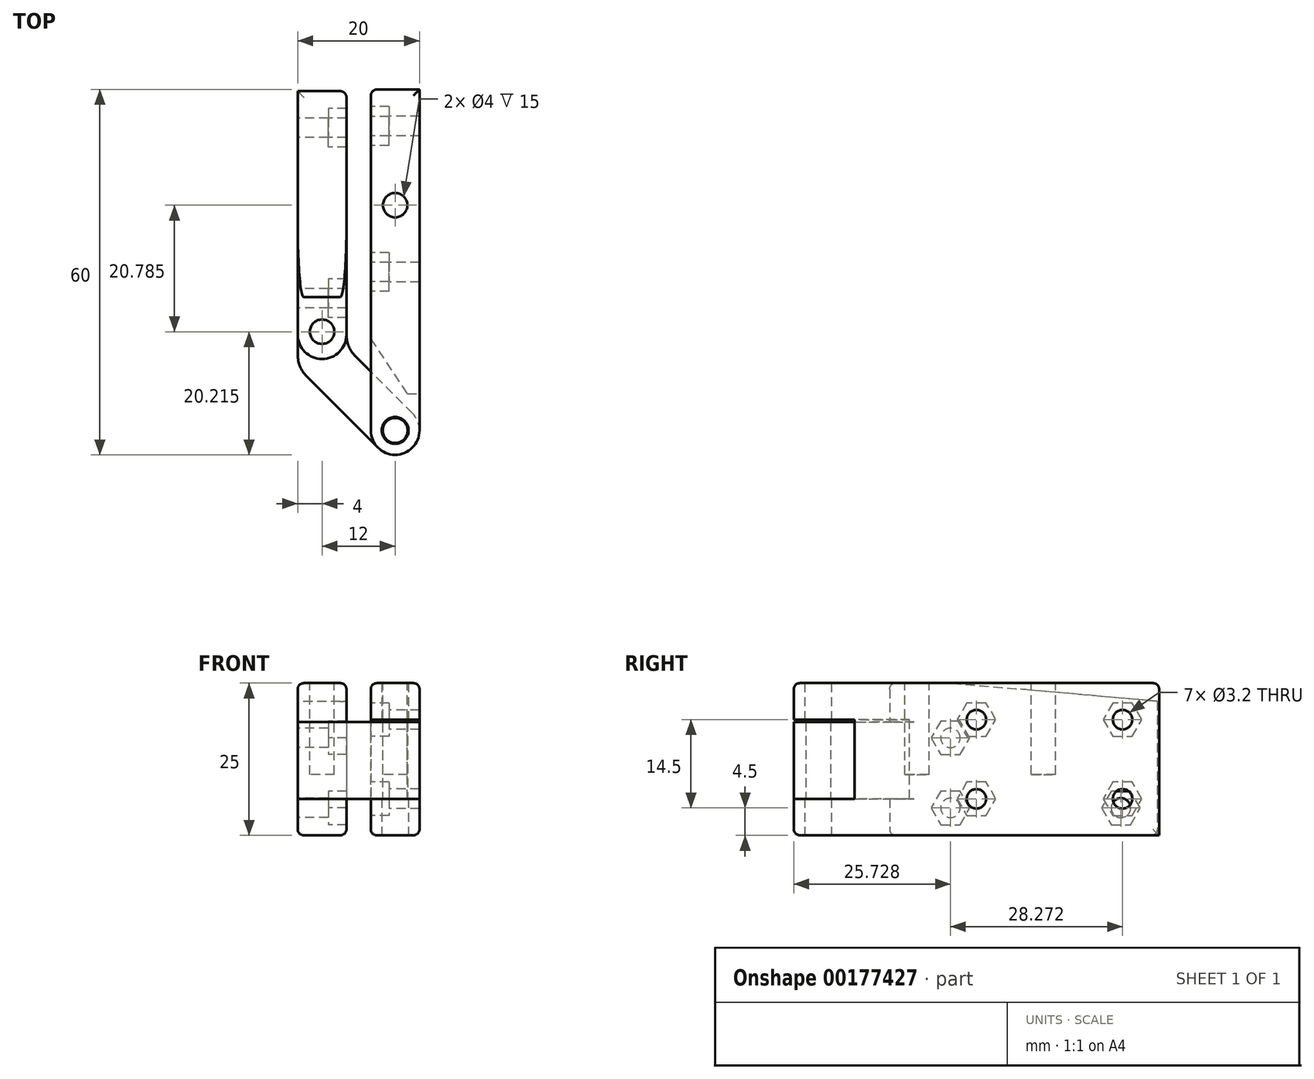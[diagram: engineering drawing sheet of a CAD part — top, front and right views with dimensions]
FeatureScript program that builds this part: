
annotation { "Feature Type Name" : "Feature", "Feature Type Description" : "" }
export const myFeature = defineFeature(function(context is Context, id is Id, definition is map)
    precondition{}
    {
        {
            var Q0;
            Q0=qCreatedBy(makeId("Top.planeOp"),FACE);
            var sketch = newSketch(context, id + "F0", { "sketchPlane" : qUnion([Q0])});
            skLineSegment(sketch, "E0", {"start": v(0, 0) * mm, "end": v(8, 0) * mm});
            skLineSegment(sketch, "E1", {"start": v(8, 0) * mm, "end": v(8, -42) * mm});
            skLineSegment(sketch, "E2", {"start": v(0, 0) * mm, "end": v(0, -42) * mm});
            skArc(sketch, "E3", {"start": v(0, -42) * mm, "mid": v(4, -46) * mm, "end": v(8, -42) * mm});
            skCircle(sketch, "E4", {"center": v(4, -42) * mm, "radius": 2.2 * mm});
            skLineSegment(sketch, "E5", {"start": v(0, 0) * mm, "end": v(0, 14) * mm});
            skLineSegment(sketch, "E6", {"start": v(0, 14) * mm, "end": v(8, 14) * mm});
            skLineSegment(sketch, "E7", {"start": v(8, 14) * mm, "end": v(8, 0) * mm});
            skSolve(sketch);
        }
        {
            var Q0;
            Q0=makeQuery(id+"F0.imprint","IMPRINT",FACE,{"disambiguationData":[TD([[makeQuery(id+"F0.imprint","IMPRINT",EDGE,{"derivedFrom":sQuery(id+"F0.wireOp",EDGE,"E0")}),-1.0]])]});
            var Q1;
            Q1=makeQuery(id+"F0.imprint","IMPRINT",FACE,{"disambiguationData":[TD([[makeQuery(id+"F0.imprint","IMPRINT",EDGE,{"derivedFrom":sQuery(id+"F0.wireOp",EDGE,"E0")}),1.0]])]});
            extrude(context, id + "F1", {"entities" : qUnion([Q0, Q1]), "depth" : 25 * mm});
        }
        {
            var Q0;
            Q0=makeQuery(id+"F1.opExtrude","SWEPT_FACE",FACE,{"disambiguationData":[OSD([sQuery(id+"F0.wireOp",EDGE,"E1")])]});
            var sketch = newSketch(context, id + "F2", { "sketchPlane" : qUnion([Q0])});
            skLineSegment(sketch, "E8", {"start": v(-46, 0) * mm, "end": v(-46, 25) * mm, "construction": true});
            skLineSegment(sketch, "E9", {"start": v(-46, 19) * mm, "end": v(-36, 19) * mm});
            skLineSegment(sketch, "E10", {"start": v(-36, 19) * mm, "end": v(-36, 6) * mm});
            skLineSegment(sketch, "E11", {"start": v(-36, 6) * mm, "end": v(-46, 6) * mm});
            skLineSegment(sketch, "E12", {"start": v(-46, 6) * mm, "end": v(-46, 19) * mm});
            skSolve(sketch);
        }
        {
            var Q0;
            Q0=qSketchRegion(id+"F2",true);
            extrude(context, id + "F3", {"entities" : qUnion([Q0]), "operationType" : NewBodyOperationType.REMOVE, "oppositeDirection" : true, "depth" : 25 * mm});
        }
        {
            var Q0;
            Q0=makeQuery(id+"F3.boolean.opBoolean","COPY",FACE,{"derivedFrom":makeQuery(id+"F3.opExtrude","SWEPT_FACE",FACE,{"disambiguationData":[OSD([sQuery(id+"F2.wireOp",EDGE,"E9")])]})});
            var sketch = newSketch(context, id + "F4", { "sketchPlane" : qUnion([Q0])});
            skLineSegment(sketch, "E13.0", {"start": v(0, 36) * mm, "end": v(8, 36) * mm, "construction": true});
            skLineSegment(sketch, "E14", {"start": v(0, 36) * mm, "end": v(0, 27) * mm});
            skLineSegment(sketch, "E15", {"start": v(0, 27) * mm, "end": v(6, 36) * mm});
            skLineSegment(sketch, "E16", {"start": v(0, 36) * mm, "end": v(6, 36) * mm});
            skSolve(sketch);
        }
        {
            var Q0;
            Q0=qSketchRegion(id+"F4",true);
            var Q1;
            Q1=makeQuery(id+"F3.boolean.opBoolean","COPY",FACE,{"derivedFrom":makeQuery(id+"F3.opExtrude","SWEPT_FACE",FACE,{"disambiguationData":[OSD([sQuery(id+"F2.wireOp",EDGE,"E11")])]})});
            extrude(context, id + "F5", {"entities" : qUnion([Q0]), "operationType" : NewBodyOperationType.REMOVE, "endBound" : BoundingType.UP_TO_SURFACE, "endBoundEntityFace" : qUnion([Q1]), "depth" : 25 * mm});
        }
        {
            var Q0;
            Q0=makeQuery(id+"F3.boolean.opBoolean","COPY",FACE,{"derivedFrom":makeQuery(id+"F3.opExtrude","SWEPT_FACE",FACE,{"disambiguationData":[OSD([sQuery(id+"F2.wireOp",EDGE,"E11")])]})});
            var sketch = newSketch(context, id + "F6", { "sketchPlane" : qUnion([Q0])});
            skCircle(sketch, "E17", {"center": v(4, -42) * mm, "radius": 2.05 * mm});
            skArc(sketch, "E18", {"start": v(1.17, -44.83) * mm, "mid": v(6.83, -44.83) * mm, "end": v(6.83, -39.17) * mm});
            skLineSegment(sketch, "E19", {"start": v(1.17, -44.83) * mm, "end": v(-10.54, -33.12) * mm});
            skLineSegment(sketch, "E20", {"start": v(6.83, -39.17) * mm, "end": v(-2.54, -29.8) * mm});
            skLineSegment(sketch, "E21", {"start": v(-12, -29.59) * mm, "end": v(-12, 0) * mm});
            skLineSegment(sketch, "E22", {"start": v(-12, 0) * mm, "end": v(-4, 0) * mm});
            skLineSegment(sketch, "E23", {"start": v(-4, 0) * mm, "end": v(-4, -26.27) * mm});
            skPoint(sketch, "E24.visualSharp", {"position": v(-4, -28.34) * mm});
            skArc(sketch, "E24.filletArc", {"start": v(-4, -26.27) * mm, "mid": v(-3.62, -28.19) * mm, "end": v(-2.54, -29.8) * mm});
            skPoint(sketch, "E25.visualSharp", {"position": v(-12, -31.66) * mm});
            skArc(sketch, "E25.filletArc", {"start": v(-12, -29.59) * mm, "mid": v(-11.62, -31.5) * mm, "end": v(-10.54, -33.12) * mm});
            skLineSegment(sketch, "E26", {"start": v(-12, 0) * mm, "end": v(-12, 13.73) * mm});
            skLineSegment(sketch, "E27", {"start": v(-12, 13.73) * mm, "end": v(-4, 13.73) * mm});
            skLineSegment(sketch, "E28", {"start": v(-4, 13.73) * mm, "end": v(-4, 0) * mm});
            skSolve(sketch);
        }
        {
            var Q0;
            Q0=qSketchRegion(id+"F6",true);
            var Q1;
            Q1=makeQuery(id+"F5.boolean.opBoolean","MERGE",FACE,{"derivedFrom":[makeQuery(id+"F3.boolean.opBoolean","COPY",FACE,{"derivedFrom":makeQuery(id+"F3.opExtrude","SWEPT_FACE",FACE,{"disambiguationData":[OSD([sQuery(id+"F2.wireOp",EDGE,"E9")])]})})],"fromTools":[makeQuery(id+"F5.opExtrude","CAP_FACE",FACE,{"disambiguationData":[OSD([sQuery(id+"F4.wireOp",EDGE,"E14"),sQuery(id+"F4.wireOp",EDGE,"E15"),sQuery(id+"F4.wireOp",EDGE,"E16")])],"isStart":true})]});
            extrude(context, id + "F7", {"entities" : qUnion([Q0]), "endBoundEntityFace" : qUnion([Q1]), "depth" : 12.6 * mm});
        }
        {
            var Q0;
            Q0=makeQuery(id+"F1.opExtrude","CAP_FACE",FACE,{"disambiguationData":[OSD([sQuery(id+"F0.wireOp",EDGE,"E0"),sQuery(id+"F0.wireOp",EDGE,"E1"),sQuery(id+"F0.wireOp",EDGE,"E2"),sQuery(id+"F0.wireOp",EDGE,"E3"),sQuery(id+"F0.wireOp",EDGE,"E4")])],"isStart":false});
            var sketch = newSketch(context, id + "F8", { "sketchPlane" : qUnion([Q0])});
            skCircle(sketch, "E29", {"center": v(4, -5) * mm, "radius": 2 * mm});
            skSolve(sketch);
        }
        {
            var Q0;
            Q0=qSketchRegion(id+"F8",true);
            extrude(context, id + "F9", {"entities" : qUnion([Q0]), "operationType" : NewBodyOperationType.REMOVE, "oppositeDirection" : true, "depth" : 15 * mm});
        }
        {
            var Q0;
            Q0=makeQuery(id+"F7.opExtrude","CAP_FACE",FACE,{"disambiguationData":[OSD([sQuery(id+"F6.wireOp",EDGE,"E17"),sQuery(id+"F6.wireOp",EDGE,"E18"),sQuery(id+"F6.wireOp",EDGE,"E19"),sQuery(id+"F6.wireOp",EDGE,"E20"),sQuery(id+"F6.wireOp",EDGE,"E21"),sQuery(id+"F6.wireOp",EDGE,"E22"),sQuery(id+"F6.wireOp",EDGE,"E23"),sQuery(id+"F6.wireOp",EDGE,"E24.filletArc"),sQuery(id+"F6.wireOp",EDGE,"E25.filletArc")])],"isStart":false});
            var sketch = newSketch(context, id + "F10", { "sketchPlane" : qUnion([Q0])});
            skLineSegment(sketch, "E30", {"start": v(-12, -29.59) * mm, "end": v(-4, -26.27) * mm});
            skLineSegment(sketch, "E31", {"start": v(-4, -26.27) * mm, "end": v(-4, -26.27) * mm});
            skLineSegment(sketch, "E32", {"start": v(-12, -26.27) * mm, "end": v(-12, -29.59) * mm});
            skArc(sketch, "E33", {"start": v(-4, -26.27) * mm, "mid": v(-8, -30.27) * mm, "end": v(-12, -26.27) * mm});
            skSolve(sketch);
        }
        {
            var Q0;
            {var subQ0=sQuery(id+"F10.wireOp",EDGE,"E33");var subQ1=sQuery(id+"F10.wireOp",EDGE,"E30");var subQ3=makeQuery(id+"F10.imprint","INTERSECT",VERTEX,{"derivedFrom":[subQ1,subQ0]});Q0=makeQuery(id+"F10.imprint","IMPRINT",FACE,{"disambiguationData":[TD([[makeQuery(id+"F10.imprint","IMPRINT",EDGE,{"disambiguationData":[TD([[subQ3,-1.0]])],"derivedFrom":subQ1}),-1.0]])]});}
            var Q1;
            {var subQ1=makeQuery(id+"F7.opExtrude","CAP_EDGE",EDGE,{"disambiguationData":[OSD([sQuery(id+"F6.wireOp",EDGE,"E27")])],"isStart":false});Q1=makeQuery(id+"F10.imprint","IMPRINT",FACE,{"disambiguationData":[TD([[makeQuery(id+"F10.imprint","IMPRINT",EDGE,{"derivedFrom":subQ1}),-1.0]])]});}
            var Q2;
            Q2=makeQuery(id+"F1.opExtrude","CAP_FACE",FACE,{"disambiguationData":[OSD([sQuery(id+"F0.wireOp",EDGE,"E0"),sQuery(id+"F0.wireOp",EDGE,"E1"),sQuery(id+"F0.wireOp",EDGE,"E2"),sQuery(id+"F0.wireOp",EDGE,"E3"),sQuery(id+"F0.wireOp",EDGE,"E4")])],"isStart":false});
            var Q3;
            Q3=makeQuery(id+"F1.opExtrude","CAP_FACE",FACE,{"disambiguationData":[OSD([sQuery(id+"F0.wireOp",EDGE,"E0"),sQuery(id+"F0.wireOp",EDGE,"E1"),sQuery(id+"F0.wireOp",EDGE,"E2"),sQuery(id+"F0.wireOp",EDGE,"E3"),sQuery(id+"F0.wireOp",EDGE,"E4")])],"isStart":true});
            extrude(context, id + "F11", {"entities" : qUnion([Q0, Q1]), "operationType" : NewBodyOperationType.ADD, "endBound" : BoundingType.UP_TO_SURFACE, "endBoundEntityFace" : qUnion([Q2]), "depth" : 25 * mm, "hasSecondDirection" : true, "secondDirectionBound" : SecondDirectionBoundingType.UP_TO_SURFACE, "secondDirectionOppositeDirection" : true, "secondDirectionBoundEntityFace" : qUnion([Q3]), "secondDirectionDepth" : 15.6 * mm});
        }
        {
            var Q0;
            Q0=makeQuery(id+"F11.opExtrude","CAP_FACE",FACE,{"disambiguationData":[OSD([sQuery(id+"F6.wireOp",EDGE,"E21"),sQuery(id+"F6.wireOp",EDGE,"E23"),sQuery(id+"F6.wireOp",EDGE,"E26"),sQuery(id+"F6.wireOp",EDGE,"E27"),sQuery(id+"F6.wireOp",EDGE,"E28"),sQuery(id+"F10.wireOp",EDGE,"E33")])],"isStart":false});
            var sketch = newSketch(context, id + "F12", { "sketchPlane" : qUnion([Q0])});
            skCircle(sketch, "E34", {"center": v(-8, -25.78) * mm, "radius": 2 * mm});
            skCircle(sketch, "E35.0", {"center": v(4, -5) * mm, "radius": 2 * mm, "construction": true});
            skLineSegment(sketch, "E36", {"start": v(-8, 2.36) * mm, "end": v(-8, -25.78) * mm, "construction": true});
            skSolve(sketch);
        }
        {
            var Q0;
            Q0=makeQuery(id+"F12.imprint","IMPRINT",FACE,{"disambiguationData":[TD([[makeQuery(id+"F12.imprint","IMPRINT",EDGE,{"derivedFrom":sQuery(id+"F12.wireOp",EDGE,"E34")}),1.0]])]});
            extrude(context, id + "F13", {"entities" : qUnion([Q0]), "operationType" : NewBodyOperationType.REMOVE, "oppositeDirection" : true, "depth" : 15 * mm});
        }
        {
            var Q0;
            {var subQ0=sQuery(id+"F6.wireOp",EDGE,"E26");var subQ1=sQuery(id+"F6.wireOp",EDGE,"E21");Q0=makeQuery(id+"F11.boolean.opBoolean","MERGE",FACE,{"derivedFrom":[makeQuery(id+"F7.opExtrude","SWEPT_FACE",FACE,{"disambiguationData":[OSD([subQ1,subQ0])]}),makeQuery(id+"F11.opExtrude","SWEPT_FACE",FACE,{"disambiguationData":[OSD([subQ1,subQ0])]})]});}
            var sketch = newSketch(context, id + "F14", { "sketchPlane" : qUnion([Q0])});
            skCircle(sketch, "E37", {"center": v(-7.73, 4.5) * mm, "radius": 1.6 * mm});
            skCircle(sketch, "E38", {"center": v(20.27, 4.5) * mm, "radius": 1.6 * mm});
            skCircle(sketch, "E39", {"center": v(20.27, 16) * mm, "radius": 1.6 * mm});
            skCircle(sketch, "E40.cCircle", {"center": v(20.27, 16) * mm, "radius": 2.75 * mm, "construction": true});
            skLineSegment(sketch, "E40.0", {"start": v(21.86, 13.25) * mm, "end": v(18.68, 13.25) * mm});
            skLineSegment(sketch, "E40.1", {"start": v(18.68, 13.25) * mm, "end": v(17.1, 16) * mm});
            skLineSegment(sketch, "E40.2", {"start": v(17.1, 16) * mm, "end": v(18.68, 18.75) * mm});
            skLineSegment(sketch, "E40.3", {"start": v(18.68, 18.75) * mm, "end": v(21.86, 18.75) * mm});
            skLineSegment(sketch, "E40.4", {"start": v(21.86, 18.75) * mm, "end": v(23.45, 16) * mm});
            skLineSegment(sketch, "E40.5", {"start": v(23.45, 16) * mm, "end": v(21.86, 13.25) * mm});
            skPoint(sketch, "E40.0.midPoint", {"position": v(20.27, 13.25) * mm});
            skCircle(sketch, "E41.cCircle", {"center": v(20.27, 4.5) * mm, "radius": 2.75 * mm, "construction": true});
            skLineSegment(sketch, "E41.0", {"start": v(21.86, 1.75) * mm, "end": v(18.68, 1.75) * mm});
            skLineSegment(sketch, "E41.1", {"start": v(18.68, 1.75) * mm, "end": v(17.1, 4.5) * mm});
            skLineSegment(sketch, "E41.2", {"start": v(17.1, 4.5) * mm, "end": v(18.68, 7.25) * mm});
            skLineSegment(sketch, "E41.3", {"start": v(18.68, 7.25) * mm, "end": v(21.86, 7.25) * mm});
            skLineSegment(sketch, "E41.4", {"start": v(21.86, 7.25) * mm, "end": v(23.45, 4.5) * mm});
            skLineSegment(sketch, "E41.5", {"start": v(23.45, 4.5) * mm, "end": v(21.86, 1.75) * mm});
            skPoint(sketch, "E41.0.midPoint", {"position": v(20.27, 1.75) * mm});
            skCircle(sketch, "E42.cCircle", {"center": v(-7.73, 4.5) * mm, "radius": 2.75 * mm, "construction": true});
            skLineSegment(sketch, "E42.0", {"start": v(-6.14, 1.75) * mm, "end": v(-9.32, 1.75) * mm});
            skLineSegment(sketch, "E42.1", {"start": v(-9.32, 1.75) * mm, "end": v(-10.9, 4.5) * mm});
            skLineSegment(sketch, "E42.2", {"start": v(-10.9, 4.5) * mm, "end": v(-9.32, 7.25) * mm});
            skLineSegment(sketch, "E42.3", {"start": v(-9.32, 7.25) * mm, "end": v(-6.14, 7.25) * mm});
            skLineSegment(sketch, "E42.4", {"start": v(-6.14, 7.25) * mm, "end": v(-4.55, 4.5) * mm});
            skLineSegment(sketch, "E42.5", {"start": v(-4.55, 4.5) * mm, "end": v(-6.14, 1.75) * mm});
            skPoint(sketch, "E42.0.midPoint", {"position": v(-7.73, 1.75) * mm});
            skLineSegment(sketch, "E43", {"start": v(-13.73, 22) * mm, "end": v(20.07, 25) * mm});
            skSolve(sketch);
        }
        {
            var Q0;
            Q0=makeQuery(id+"F14.imprint","IMPRINT",FACE,{"disambiguationData":[TD([[makeQuery(id+"F14.imprint","IMPRINT",EDGE,{"derivedFrom":sQuery(id+"F14.wireOp",EDGE,"E37")}),1.0]])]});
            var Q1;
            Q1=makeQuery(id+"F14.imprint","IMPRINT",FACE,{"disambiguationData":[TD([[makeQuery(id+"F14.imprint","IMPRINT",EDGE,{"derivedFrom":sQuery(id+"F14.wireOp",EDGE,"E37")}),-1.0]])]});
            var Q2;
            Q2=makeQuery(id+"F14.imprint","IMPRINT",FACE,{"disambiguationData":[TD([[makeQuery(id+"F14.imprint","IMPRINT",EDGE,{"derivedFrom":sQuery(id+"F14.wireOp",EDGE,"E38")}),-1.0]])]});
            var Q3;
            Q3=makeQuery(id+"F14.imprint","IMPRINT",FACE,{"disambiguationData":[TD([[makeQuery(id+"F14.imprint","IMPRINT",EDGE,{"derivedFrom":sQuery(id+"F14.wireOp",EDGE,"E38")}),1.0]])]});
            var Q4;
            Q4=makeQuery(id+"F14.imprint","IMPRINT",FACE,{"disambiguationData":[TD([[makeQuery(id+"F14.imprint","IMPRINT",EDGE,{"derivedFrom":sQuery(id+"F14.wireOp",EDGE,"E39")}),1.0]])]});
            var Q5;
            Q5=makeQuery(id+"F14.imprint","IMPRINT",FACE,{"disambiguationData":[TD([[makeQuery(id+"F14.imprint","IMPRINT",EDGE,{"derivedFrom":sQuery(id+"F14.wireOp",EDGE,"E39")}),-1.0]])]});
            var Q6;
            {var subQ0=sQuery(id+"F14.wireOp",EDGE,"E43");Q6=makeQuery(id+"F14.imprint","IMPRINT",FACE,{"disambiguationData":[TD([[makeQuery(id+"F14.imprint","IMPRINT",EDGE,{"derivedFrom":subQ0}),1.0]])]});}
            extrude(context, id + "F15", {"entities" : qUnion([Q0, Q1, Q2, Q3, Q4, Q5, Q6]), "operationType" : NewBodyOperationType.REMOVE, "endBound" : BoundingType.UP_TO_NEXT, "oppositeDirection" : true, "depth" : 25 * mm});
        }
        {
            var Q0;
            Q0=makeQuery(id+"F14.imprint","IMPRINT",FACE,{"disambiguationData":[TD([[makeQuery(id+"F14.imprint","IMPRINT",EDGE,{"derivedFrom":sQuery(id+"F14.wireOp",EDGE,"E39")}),-1.0]])]});
            var Q1;
            Q1=makeQuery(id+"F14.imprint","IMPRINT",FACE,{"disambiguationData":[TD([[makeQuery(id+"F14.imprint","IMPRINT",EDGE,{"derivedFrom":sQuery(id+"F14.wireOp",EDGE,"E38")}),-1.0]])]});
            var Q2;
            Q2=makeQuery(id+"F14.imprint","IMPRINT",FACE,{"disambiguationData":[TD([[makeQuery(id+"F14.imprint","IMPRINT",EDGE,{"derivedFrom":sQuery(id+"F14.wireOp",EDGE,"E37")}),-1.0]])]});
            extrude(context, id + "F16", {"entities" : qUnion([Q0, Q1, Q2]), "operationType" : NewBodyOperationType.ADD, "oppositeDirection" : true, "depth" : 5 * mm});
        }
        {
            var Q0;
            Q0=makeQuery(id+"F1.opExtrude","SWEPT_FACE",FACE,{"disambiguationData":[OSD([sQuery(id+"F0.wireOp",EDGE,"E2"),sQuery(id+"F0.wireOp",EDGE,"E5")])]});
            var sketch = newSketch(context, id + "F17", { "sketchPlane" : qUnion([Q0])});
            skCircle(sketch, "E44", {"center": v(-8, 19) * mm, "radius": 1.6 * mm});
            skCircle(sketch, "E45", {"center": v(-8, 6) * mm, "radius": 1.6 * mm});
            skCircle(sketch, "E46", {"center": v(16, 6) * mm, "radius": 1.6 * mm});
            skCircle(sketch, "E47", {"center": v(16, 19) * mm, "radius": 1.6 * mm});
            skCircle(sketch, "E48.cCircle", {"center": v(-8, 19) * mm, "radius": 2.75 * mm, "construction": true});
            skLineSegment(sketch, "E48.0", {"start": v(-6.41, 16.25) * mm, "end": v(-9.59, 16.25) * mm});
            skLineSegment(sketch, "E48.1", {"start": v(-9.59, 16.25) * mm, "end": v(-11.18, 19) * mm});
            skLineSegment(sketch, "E48.2", {"start": v(-11.18, 19) * mm, "end": v(-9.59, 21.75) * mm});
            skLineSegment(sketch, "E48.3", {"start": v(-9.59, 21.75) * mm, "end": v(-6.41, 21.75) * mm});
            skLineSegment(sketch, "E48.4", {"start": v(-6.41, 21.75) * mm, "end": v(-4.82, 19) * mm});
            skLineSegment(sketch, "E48.5", {"start": v(-4.82, 19) * mm, "end": v(-6.41, 16.25) * mm});
            skPoint(sketch, "E48.0.midPoint", {"position": v(-8, 16.25) * mm});
            skCircle(sketch, "E49.cCircle", {"center": v(-8, 6) * mm, "radius": 2.75 * mm, "construction": true});
            skLineSegment(sketch, "E49.0", {"start": v(-6.41, 3.25) * mm, "end": v(-9.59, 3.25) * mm});
            skLineSegment(sketch, "E49.1", {"start": v(-9.59, 3.25) * mm, "end": v(-11.18, 6) * mm});
            skLineSegment(sketch, "E49.2", {"start": v(-11.18, 6) * mm, "end": v(-9.59, 8.75) * mm});
            skLineSegment(sketch, "E49.3", {"start": v(-9.59, 8.75) * mm, "end": v(-6.41, 8.75) * mm});
            skLineSegment(sketch, "E49.4", {"start": v(-6.41, 8.75) * mm, "end": v(-4.82, 6) * mm});
            skLineSegment(sketch, "E49.5", {"start": v(-4.82, 6) * mm, "end": v(-6.41, 3.25) * mm});
            skPoint(sketch, "E49.0.midPoint", {"position": v(-8, 3.25) * mm});
            skCircle(sketch, "E50.cCircle", {"center": v(16, 6) * mm, "radius": 2.75 * mm, "construction": true});
            skLineSegment(sketch, "E50.0", {"start": v(17.59, 3.25) * mm, "end": v(14.41, 3.25) * mm});
            skLineSegment(sketch, "E50.1", {"start": v(14.41, 3.25) * mm, "end": v(12.82, 6) * mm});
            skLineSegment(sketch, "E50.2", {"start": v(12.82, 6) * mm, "end": v(14.41, 8.75) * mm});
            skLineSegment(sketch, "E50.3", {"start": v(14.41, 8.75) * mm, "end": v(17.59, 8.75) * mm});
            skLineSegment(sketch, "E50.4", {"start": v(17.59, 8.75) * mm, "end": v(19.18, 6) * mm});
            skLineSegment(sketch, "E50.5", {"start": v(19.18, 6) * mm, "end": v(17.59, 3.25) * mm});
            skPoint(sketch, "E50.0.midPoint", {"position": v(16, 3.25) * mm});
            skCircle(sketch, "E51.cCircle", {"center": v(16, 19) * mm, "radius": 2.75 * mm, "construction": true});
            skLineSegment(sketch, "E51.0", {"start": v(17.59, 16.25) * mm, "end": v(14.41, 16.25) * mm});
            skLineSegment(sketch, "E51.1", {"start": v(14.41, 16.25) * mm, "end": v(12.82, 19) * mm});
            skLineSegment(sketch, "E51.2", {"start": v(12.82, 19) * mm, "end": v(14.41, 21.75) * mm});
            skLineSegment(sketch, "E51.3", {"start": v(14.41, 21.75) * mm, "end": v(17.59, 21.75) * mm});
            skLineSegment(sketch, "E51.4", {"start": v(17.59, 21.75) * mm, "end": v(19.18, 19) * mm});
            skLineSegment(sketch, "E51.5", {"start": v(19.18, 19) * mm, "end": v(17.59, 16.25) * mm});
            skPoint(sketch, "E51.0.midPoint", {"position": v(16, 16.25) * mm});
            skSolve(sketch);
        }
        {
            var Q0;
            Q0=makeQuery(id+"F17.imprint","IMPRINT",FACE,{"disambiguationData":[TD([[makeQuery(id+"F17.imprint","IMPRINT",EDGE,{"derivedFrom":sQuery(id+"F17.wireOp",EDGE,"E44")}),1.0]])]});
            var Q1;
            Q1=makeQuery(id+"F17.imprint","IMPRINT",FACE,{"disambiguationData":[TD([[makeQuery(id+"F17.imprint","IMPRINT",EDGE,{"derivedFrom":sQuery(id+"F17.wireOp",EDGE,"E47")}),1.0]])]});
            var Q2;
            Q2=makeQuery(id+"F17.imprint","IMPRINT",FACE,{"disambiguationData":[TD([[makeQuery(id+"F17.imprint","IMPRINT",EDGE,{"derivedFrom":sQuery(id+"F17.wireOp",EDGE,"E46")}),1.0]])]});
            var Q3;
            Q3=makeQuery(id+"F17.imprint","IMPRINT",FACE,{"disambiguationData":[TD([[makeQuery(id+"F17.imprint","IMPRINT",EDGE,{"derivedFrom":sQuery(id+"F17.wireOp",EDGE,"E45")}),1.0]])]});
            extrude(context, id + "F18", {"entities" : qUnion([Q0, Q1, Q2, Q3]), "operationType" : NewBodyOperationType.REMOVE, "endBound" : BoundingType.UP_TO_NEXT, "oppositeDirection" : true, "depth" : 25 * mm});
        }
        {
            var Q0;
            Q0=makeQuery(id+"F17.imprint","IMPRINT",FACE,{"disambiguationData":[TD([[makeQuery(id+"F17.imprint","IMPRINT",EDGE,{"derivedFrom":sQuery(id+"F17.wireOp",EDGE,"E44")}),-1.0]])]});
            var Q1;
            Q1=makeQuery(id+"F17.imprint","IMPRINT",FACE,{"disambiguationData":[TD([[makeQuery(id+"F17.imprint","IMPRINT",EDGE,{"derivedFrom":sQuery(id+"F17.wireOp",EDGE,"E45")}),-1.0]])]});
            var Q2;
            Q2=makeQuery(id+"F17.imprint","IMPRINT",FACE,{"disambiguationData":[TD([[makeQuery(id+"F17.imprint","IMPRINT",EDGE,{"derivedFrom":sQuery(id+"F17.wireOp",EDGE,"E46")}),-1.0]])]});
            var Q3;
            Q3=makeQuery(id+"F17.imprint","IMPRINT",FACE,{"disambiguationData":[TD([[makeQuery(id+"F17.imprint","IMPRINT",EDGE,{"derivedFrom":sQuery(id+"F17.wireOp",EDGE,"E47")}),-1.0]])]});
            extrude(context, id + "F19", {"entities" : qUnion([Q0, Q1, Q2, Q3]), "operationType" : NewBodyOperationType.REMOVE, "oppositeDirection" : true, "depth" : 3 * mm});
        }
        {
            var Q0;
            Q0=makeQuery(id+"F15.boolean.opBoolean","COPY",EDGE,{"derivedFrom":makeQuery(id+"F15.opExtrude","SWEPT_EDGE",EDGE,{"disambiguationData":[OSD([sQuery(id+"F6.wireOp",EDGE,"E21"),sQuery(id+"F6.wireOp",EDGE,"E26"),sQuery(id+"F6.wireOp",EDGE,"E27"),sQuery(id+"F14.wireOp",EDGE,"E43")])]})});
            var Q1;
            Q1=makeQuery(id+"F11.opExtrude","CAP_EDGE",EDGE,{"disambiguationData":[OSD([sQuery(id+"F6.wireOp",EDGE,"E27")])],"isStart":true});
            var Q2;
            {var subQ0=sQuery(id+"F6.wireOp",EDGE,"E27");var subQ1=sQuery(id+"F6.wireOp",EDGE,"E28");Q2=makeQuery(id+"F11.boolean.opBoolean","MERGE",EDGE,{"derivedFrom":[makeQuery(id+"F7.opExtrude","SWEPT_EDGE",EDGE,{"disambiguationData":[OSD([subQ0,subQ1])]}),makeQuery(id+"F11.opExtrude","TWEAK_EDGE",EDGE,{"derivedFrom":[makeQuery(id+"F10.imprint","IMPRINT",EDGE,{"derivedFrom":makeQuery(id+"F7.opExtrude","CAP_EDGE",EDGE,{"disambiguationData":[OSD([sQuery(id+"F6.wireOp",EDGE,"E23"),subQ1])],"isStart":false})}),makeQuery(id+"F10.imprint","IMPRINT",EDGE,{"derivedFrom":makeQuery(id+"F7.opExtrude","CAP_EDGE",EDGE,{"disambiguationData":[OSD([subQ0])],"isStart":false})})]})]});}
            var Q3;
            Q3=makeQuery(id+"F11.opExtrude","CAP_EDGE",EDGE,{"disambiguationData":[OSD([sQuery(id+"F6.wireOp",EDGE,"E23"),sQuery(id+"F6.wireOp",EDGE,"E28")])],"isStart":true});
            var Q4;
            Q4=makeQuery(id+"F15.boolean.opBoolean","COPY",EDGE,{"derivedFrom":makeQuery(id+"F15.opExtrude","CAP_EDGE",EDGE,{"disambiguationData":[OSD([sQuery(id+"F14.wireOp",EDGE,"E43")])],"isStart":false})});
            var Q5;
            Q5=makeQuery(id+"F1.opExtrude","SWEPT_EDGE",EDGE,{"disambiguationData":[OSD([sQuery(id+"F0.wireOp",EDGE,"E5"),sQuery(id+"F0.wireOp",EDGE,"E6")])]});
            var Q6;
            Q6=makeQuery(id+"F1.opExtrude","CAP_EDGE",EDGE,{"disambiguationData":[OSD([sQuery(id+"F0.wireOp",EDGE,"E6")])],"isStart":false});
            var Q7;
            Q7=makeQuery(id+"F1.opExtrude","CAP_EDGE",EDGE,{"disambiguationData":[OSD([sQuery(id+"F0.wireOp",EDGE,"E2"),sQuery(id+"F0.wireOp",EDGE,"E5")])],"isStart":false});
            var Q8;
            Q8=makeQuery(id+"F1.opExtrude","CAP_EDGE",EDGE,{"disambiguationData":[OSD([sQuery(id+"F0.wireOp",EDGE,"E2"),sQuery(id+"F0.wireOp",EDGE,"E5")])],"isStart":true});
            var Q9;
            Q9=makeQuery(id+"F15.boolean.opBoolean","COPY",EDGE,{"derivedFrom":makeQuery(id+"F15.opExtrude","CAP_EDGE",EDGE,{"disambiguationData":[OSD([sQuery(id+"F14.wireOp",EDGE,"E43")])],"isStart":true})});
            var Q10;
            Q10=makeQuery(id+"F11.opExtrude","CAP_EDGE",EDGE,{"disambiguationData":[OSD([sQuery(id+"F10.wireOp",EDGE,"E33")])],"isStart":false});
            fillet(context, id + "F20", {"entities" : qUnion([Q0, Q1, Q2, Q3, Q4, Q5, Q6, Q7, Q8, Q9, Q10]), "radius" : 1 * mm, "tangentPropagation" : true, "allowEdgeOverflow" : false});
        }
    });
